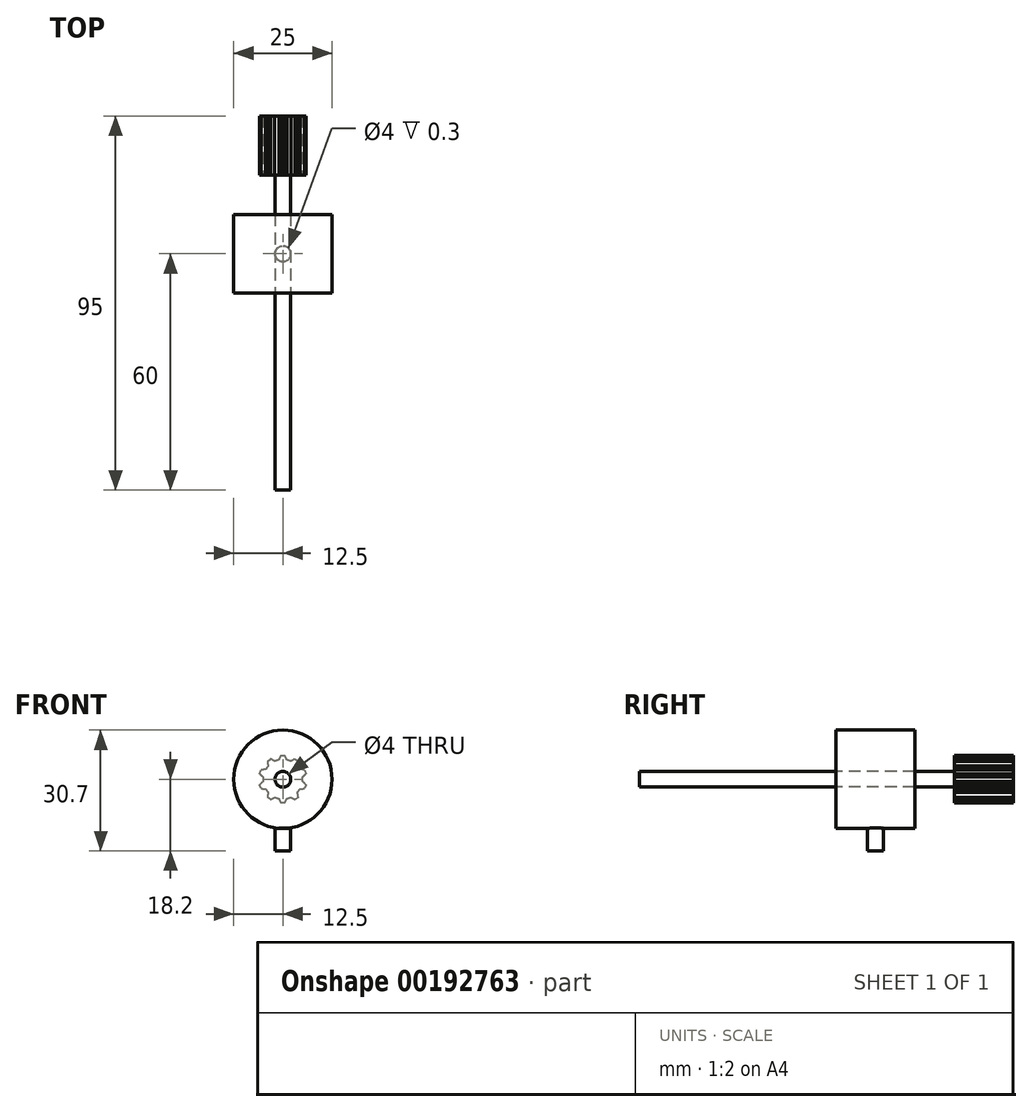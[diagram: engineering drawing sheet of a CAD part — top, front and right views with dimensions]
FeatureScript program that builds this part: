
annotation { "Feature Type Name" : "Feature", "Feature Type Description" : "" }
export const myFeature = defineFeature(function(context is Context, id is Id, definition is map)
    precondition{}
    {
        {
            var Q0;
            Q0=qCreatedBy(makeId("Front.planeOp"),FACE);
            var sketch = newSketch(context, id + "F0", { "sketchPlane" : qUnion([Q0])});
            skCircle(sketch, "E0", {"center": v(0, 0) * mm, "radius": 12.5 * mm});
            skSolve(sketch);
        }
        {
            var Q0;
            Q0 = qSketchRegion(id + "F0", true);
            extrude(context, id + "F1", {"entities" : qUnion([Q0]), "depth" : 10 * mm, "hasSecondDirection" : true, "secondDirectionOppositeDirection" : true, "secondDirectionDepth" : 10 * mm});
        }
        {
            var Q0;
            Q0=makeQuery(id+"F1.opExtrude","CAP_FACE",FACE,{"disambiguationData":[OSD([sQuery(id+"F0.wireOp",EDGE,"E0")])],"isStart":false});
            var sketch = newSketch(context, id + "F2", { "sketchPlane" : qUnion([Q0])});
            skCircle(sketch, "E1", {"center": v(0, 0) * mm, "radius": 2 * mm});
            skSolve(sketch);
        }
        {
            var Q0;
            Q0 = qSketchRegion(id + "F2", true);
            var Q1;
            Q1=makeQuery(id+"F1.opExtrude","CAP_FACE",FACE,{"disambiguationData":[OSD([sQuery(id+"F0.wireOp",EDGE,"E0")])],"isStart":true});
            extrude(context, id + "F3", {"entities" : qUnion([Q0]), "operationType" : NewBodyOperationType.REMOVE, "endBound" : BoundingType.UP_TO_SURFACE, "oppositeDirection" : true, "endBoundEntityFace" : qUnion([Q1]), "depth" : 40 * mm});
        }
        {
            var Q0;
            Q0=makeQuery(id+"F1.opExtrude","CAP_FACE",FACE,{"disambiguationData":[OSD([sQuery(id+"F0.wireOp",EDGE,"E0")])],"isStart":true});
            var sketch = newSketch(context, id + "F4", { "sketchPlane" : qUnion([Q0])});
            skCircle(sketch, "E2", {"center": v(0, 0) * mm, "radius": 2 * mm});
            skSolve(sketch);
        }
        {
            var Q0;
            Q0 = qSketchRegion(id + "F4", true);
            extrude(context, id + "F5", {"entities" : qUnion([Q0]), "depth" : 10 * mm, "hasSecondDirection" : true, "secondDirectionOppositeDirection" : true, "secondDirectionDepth" : 70 * mm});
        }
        {
            var Q0;
            Q0=makeQuery(id+"F5.opExtrude","CAP_FACE",FACE,{"disambiguationData":[OSD([sQuery(id+"F4.wireOp",EDGE,"E2")])],"isStart":false});
            var sketch = newSketch(context, id + "F6", { "sketchPlane" : qUnion([Q0])});
            skCircle(sketch, "E3", {"center": v(0, 0) * mm, "radius": 5 * mm});
            skLineSegment(sketch, "E4", {"start": v(0, 0) * mm, "end": v(0, 6) * mm, "construction": true});
            skLineSegment(sketch, "E5", {"start": v(0, 6) * mm, "end": v(-0.5, 6) * mm});
            skArc(sketch, "E6", {"start": v(-0.5, 6) * mm, "mid": v(-0.78, 5.46) * mm, "end": v(-1.02, 4.9) * mm});
            skLineSegment(sketch, "E7.MirrorCS", {"start": v(0, 6) * mm, "end": v(0.5, 6) * mm});
            skArc(sketch, "E8.MirrorCS", {"start": v(0.5, 6) * mm, "mid": v(0.78, 5.46) * mm, "end": v(1.02, 4.9) * mm});
            skArc(sketch, "E9.1.1", {"start": v(-3.93, 4.56) * mm, "mid": v(-3.84, 3.96) * mm, "end": v(-3.7, 3.36) * mm});
            skLineSegment(sketch, "E9.1.2", {"start": v(-3.53, 4.85) * mm, "end": v(-3.93, 4.56) * mm});
            skLineSegment(sketch, "E9.1.3", {"start": v(-3.53, 4.85) * mm, "end": v(-3.12, 5.15) * mm});
            skArc(sketch, "E9.1.4", {"start": v(-3.12, 5.15) * mm, "mid": v(-2.57, 4.88) * mm, "end": v(-2.05, 4.56) * mm});
            skArc(sketch, "E9.2.1", {"start": v(-5.86, 1.38) * mm, "mid": v(-5.43, 0.94) * mm, "end": v(-4.97, 0.54) * mm});
            skLineSegment(sketch, "E9.2.2", {"start": v(-5.7, 1.85) * mm, "end": v(-5.86, 1.38) * mm});
            skLineSegment(sketch, "E9.2.3", {"start": v(-5.7, 1.85) * mm, "end": v(-5.55, 2.33) * mm});
            skArc(sketch, "E9.2.4", {"start": v(-5.55, 2.33) * mm, "mid": v(-4.95, 2.43) * mm, "end": v(-4.34, 2.48) * mm});
            skArc(sketch, "E10.2.3.0", {"start": v(-5.55, -2.33) * mm, "mid": v(-4.95, -2.43) * mm, "end": v(-4.34, -2.48) * mm});
            skLineSegment(sketch, "E10.6.3.0", {"start": v(-5.7, -1.85) * mm, "end": v(-5.55, -2.33) * mm});
            skLineSegment(sketch, "E10.9.3.0", {"start": v(-5.7, -1.85) * mm, "end": v(-5.86, -1.38) * mm});
            skArc(sketch, "E10.12.3.0", {"start": v(-5.86, -1.38) * mm, "mid": v(-5.43, -0.94) * mm, "end": v(-4.97, -0.54) * mm});
            skArc(sketch, "E10.2.4.0", {"start": v(-3.12, -5.15) * mm, "mid": v(-2.57, -4.88) * mm, "end": v(-2.05, -4.56) * mm});
            skLineSegment(sketch, "E10.6.4.0", {"start": v(-3.53, -4.85) * mm, "end": v(-3.12, -5.15) * mm});
            skLineSegment(sketch, "E10.9.4.0", {"start": v(-3.53, -4.85) * mm, "end": v(-3.93, -4.56) * mm});
            skArc(sketch, "E10.12.4.0", {"start": v(-3.93, -4.56) * mm, "mid": v(-3.84, -3.96) * mm, "end": v(-3.7, -3.36) * mm});
            skArc(sketch, "E10.2.5.0", {"start": v(0.5, -6) * mm, "mid": v(0.78, -5.46) * mm, "end": v(1.02, -4.9) * mm});
            skLineSegment(sketch, "E10.6.5.0", {"start": v(0, -6) * mm, "end": v(0.5, -6) * mm});
            skLineSegment(sketch, "E10.9.5.0", {"start": v(0, -6) * mm, "end": v(-0.5, -6) * mm});
            skArc(sketch, "E10.12.5.0", {"start": v(-0.5, -6) * mm, "mid": v(-0.78, -5.46) * mm, "end": v(-1.02, -4.9) * mm});
            skArc(sketch, "E10.2.6.0", {"start": v(3.93, -4.56) * mm, "mid": v(3.84, -3.96) * mm, "end": v(3.7, -3.36) * mm});
            skLineSegment(sketch, "E10.6.6.0", {"start": v(3.53, -4.85) * mm, "end": v(3.93, -4.56) * mm});
            skLineSegment(sketch, "E10.9.6.0", {"start": v(3.53, -4.85) * mm, "end": v(3.12, -5.15) * mm});
            skArc(sketch, "E10.12.6.0", {"start": v(3.12, -5.15) * mm, "mid": v(2.57, -4.88) * mm, "end": v(2.05, -4.56) * mm});
            skArc(sketch, "E10.2.7.0", {"start": v(5.86, -1.38) * mm, "mid": v(5.43, -0.94) * mm, "end": v(4.97, -0.54) * mm});
            skLineSegment(sketch, "E10.6.7.0", {"start": v(5.7, -1.85) * mm, "end": v(5.86, -1.38) * mm});
            skLineSegment(sketch, "E10.9.7.0", {"start": v(5.7, -1.85) * mm, "end": v(5.55, -2.33) * mm});
            skArc(sketch, "E10.12.7.0", {"start": v(5.55, -2.33) * mm, "mid": v(4.95, -2.43) * mm, "end": v(4.34, -2.48) * mm});
            skArc(sketch, "E11.2.8.0", {"start": v(5.55, 2.33) * mm, "mid": v(4.95, 2.43) * mm, "end": v(4.34, 2.48) * mm});
            skLineSegment(sketch, "E11.6.8.0", {"start": v(5.7, 1.85) * mm, "end": v(5.55, 2.33) * mm});
            skLineSegment(sketch, "E11.9.8.0", {"start": v(5.7, 1.85) * mm, "end": v(5.86, 1.38) * mm});
            skArc(sketch, "E11.12.8.0", {"start": v(5.86, 1.38) * mm, "mid": v(5.43, 0.94) * mm, "end": v(4.97, 0.54) * mm});
            skArc(sketch, "E11.2.9.0", {"start": v(3.12, 5.15) * mm, "mid": v(2.57, 4.88) * mm, "end": v(2.05, 4.56) * mm});
            skLineSegment(sketch, "E11.6.9.0", {"start": v(3.53, 4.85) * mm, "end": v(3.12, 5.15) * mm});
            skLineSegment(sketch, "E11.9.9.0", {"start": v(3.53, 4.85) * mm, "end": v(3.93, 4.56) * mm});
            skArc(sketch, "E11.12.9.0", {"start": v(3.93, 4.56) * mm, "mid": v(3.84, 3.96) * mm, "end": v(3.7, 3.36) * mm});
            skSolve(sketch);
        }
        {
            var Q0;
            Q0 = qSketchRegion(id + "F6", true);
            extrude(context, id + "F7", {"entities" : qUnion([Q0]), "operationType" : NewBodyOperationType.ADD, "depth" : 15 * mm});
        }
        {
            var Q0;
            Q0=qCreatedBy(makeId("Top.planeOp"),FACE);
            var sketch = newSketch(context, id + "F8", { "sketchPlane" : qUnion([Q0])});
            skCircle(sketch, "E12", {"center": v(0, 0) * mm, "radius": 2 * mm});
            skSolve(sketch);
        }
        {
            var Q0;
            Q0 = qSketchRegion(id + "F8", true);
            extrude(context, id + "F9", {"entities" : qUnion([Q0]), "depth" : 6 * mm});
        }
        {
            var Q0;
            Q0=makeQuery(id+"F9.opExtrude","SWEPT_BODY",BODY,{"disambiguationData":[OSD([sQuery(id+"F8.wireOp",EDGE,"E12")])]});
            transform(context, id + "F10", {"entities" : qUnion([Q0]), "transformType" : TransformType.TRANSLATION_3D, "dx" : 0 * mm, "dy" : 0 * mm, "dz" : -18.2 * mm, "makeCopy" : false});
        }
        {
            var Q0;
            Q0=makeQuery(id+"F9.opExtrude","SWEPT_BODY",BODY,{"disambiguationData":[OSD([sQuery(id+"F8.wireOp",EDGE,"E12")])]});
            var Q1;
            Q1=makeQuery(id+"F1.opExtrude","SWEPT_BODY",BODY,{"disambiguationData":[OSD([sQuery(id+"F0.wireOp",EDGE,"E0")])]});
            booleanBodies(context, id + "F11", {"operationType" : BooleanOperationType.SUBTRACTION, "tools" : qUnion([Q0]), "targets" : qUnion([Q1]), "keepTools" : true});
        }
    });
